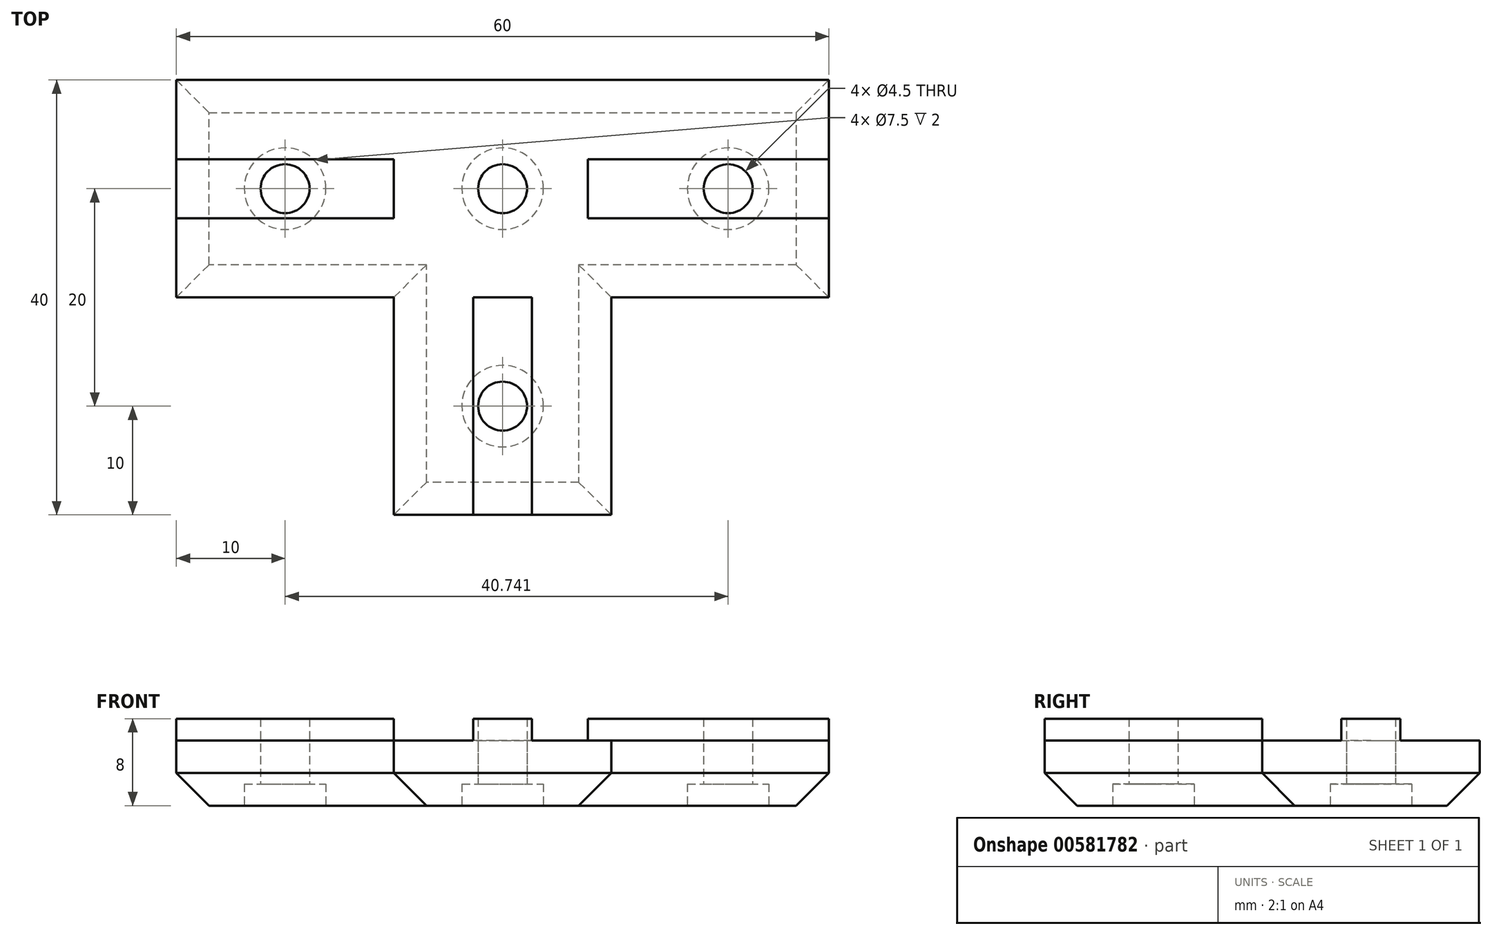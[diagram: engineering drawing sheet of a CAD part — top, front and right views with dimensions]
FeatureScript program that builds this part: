
annotation { "Feature Type Name" : "Feature", "Feature Type Description" : "" }
export const myFeature = defineFeature(function(context is Context, id is Id, definition is map)
    precondition{}
    {
        {
            var Q0;
            Q0=qCreatedBy(makeId("Top.planeOp"),FACE);
            var sketch = newSketch(context, id + "F0", { "sketchPlane" : qUnion([Q0])});
            skLineSegment(sketch, "E0", {"start": v(0, 0) * mm, "end": v(0, 20) * mm, "construction": true});
            skLineSegment(sketch, "E1", {"start": v(0, 0) * mm, "end": v(0, -20) * mm, "construction": true});
            skLineSegment(sketch, "E2", {"start": v(-10, 0) * mm, "end": v(-30, 0) * mm});
            skLineSegment(sketch, "E3", {"start": v(0, 20) * mm, "end": v(-30, 20) * mm});
            skLineSegment(sketch, "E4", {"start": v(-30, 20) * mm, "end": v(-30, 0) * mm});
            skLineSegment(sketch, "E5", {"start": v(0, 20) * mm, "end": v(30, 20) * mm});
            skLineSegment(sketch, "E6", {"start": v(30, 20) * mm, "end": v(30, 0) * mm});
            skLineSegment(sketch, "E7", {"start": v(30, 0) * mm, "end": v(10, 0) * mm});
            skLineSegment(sketch, "E8", {"start": v(0, -20) * mm, "end": v(10, -20) * mm});
            skLineSegment(sketch, "E9", {"start": v(10, -20) * mm, "end": v(10, 0) * mm});
            skLineSegment(sketch, "E10", {"start": v(0, -20) * mm, "end": v(-10, -20) * mm});
            skLineSegment(sketch, "E11", {"start": v(-10, -20) * mm, "end": v(-10, 0) * mm});
            skSolve(sketch);
        }
        {
            var Q0;
            Q0=qSketchRegion(id+"F0",true);
            extrude(context, id + "F1", {"entities" : qUnion([Q0]), "depth" : 6 * mm});
        }
        {
            var Q0;
            Q0=makeQuery(id+"F1.opExtrude","CAP_FACE",FACE,{"disambiguationData":[OSD([sQuery(id+"F0.wireOp",EDGE,"E2"),sQuery(id+"F0.wireOp",EDGE,"E3"),sQuery(id+"F0.wireOp",EDGE,"E4"),sQuery(id+"F0.wireOp",EDGE,"E5"),sQuery(id+"F0.wireOp",EDGE,"E6"),sQuery(id+"F0.wireOp",EDGE,"E7"),sQuery(id+"F0.wireOp",EDGE,"E8"),sQuery(id+"F0.wireOp",EDGE,"E9"),sQuery(id+"F0.wireOp",EDGE,"E10"),sQuery(id+"F0.wireOp",EDGE,"E11")])],"isStart":false});
            var sketch = newSketch(context, id + "F2", { "sketchPlane" : qUnion([Q0])});
            skLineSegment(sketch, "E12", {"start": v(-30, 10) * mm, "end": v(30, 10) * mm, "construction": true});
            skLineSegment(sketch, "E13", {"start": v(0, -20) * mm, "end": v(0, 0) * mm, "construction": true});
            skLineSegment(sketch, "E14", {"start": v(0, 0) * mm, "end": v(-2.71, 0) * mm});
            skLineSegment(sketch, "E15", {"start": v(-2.71, 0) * mm, "end": v(-2.7, -20) * mm});
            skLineSegment(sketch, "E16", {"start": v(2.71, -20) * mm, "end": v(2.71, 0) * mm});
            skLineSegment(sketch, "E17", {"start": v(2.71, 0) * mm, "end": v(0, 0) * mm});
            skLineSegment(sketch, "E18", {"start": v(-2.7, -20) * mm, "end": v(2.71, -20) * mm});
            skLineSegment(sketch, "E19", {"start": v(7.85, 10) * mm, "end": v(7.85, 12.71) * mm});
            skLineSegment(sketch, "E20", {"start": v(7.85, 12.71) * mm, "end": v(30, 12.71) * mm});
            skLineSegment(sketch, "E21", {"start": v(30, 12.71) * mm, "end": v(30, 7.3) * mm});
            skLineSegment(sketch, "E22", {"start": v(30, 7.3) * mm, "end": v(7.85, 7.29) * mm});
            skLineSegment(sketch, "E23", {"start": v(7.85, 7.29) * mm, "end": v(7.85, 10) * mm});
            skLineSegment(sketch, "E24", {"start": v(-30, 12.71) * mm, "end": v(-30, 7.29) * mm});
            skLineSegment(sketch, "E25", {"start": v(-30, 7.29) * mm, "end": v(-10, 7.29) * mm});
            skLineSegment(sketch, "E26", {"start": v(-10, 7.29) * mm, "end": v(-10, 12.71) * mm});
            skLineSegment(sketch, "E27", {"start": v(-10, 12.71) * mm, "end": v(-30, 12.71) * mm});
            skSolve(sketch);
        }
        {
            var Q0;
            Q0=qSketchRegion(id+"F2",true);
            extrude(context, id + "F3", {"entities" : qUnion([Q0]), "operationType" : NewBodyOperationType.ADD, "depth" : 2 * mm});
        }
        {
            var Q0;
            Q0=makeQuery(id+"F1.opExtrude","CAP_FACE",FACE,{"disambiguationData":[OSD([sQuery(id+"F0.wireOp",EDGE,"E2"),sQuery(id+"F0.wireOp",EDGE,"E3"),sQuery(id+"F0.wireOp",EDGE,"E4"),sQuery(id+"F0.wireOp",EDGE,"E5"),sQuery(id+"F0.wireOp",EDGE,"E6"),sQuery(id+"F0.wireOp",EDGE,"E7"),sQuery(id+"F0.wireOp",EDGE,"E8"),sQuery(id+"F0.wireOp",EDGE,"E9"),sQuery(id+"F0.wireOp",EDGE,"E10"),sQuery(id+"F0.wireOp",EDGE,"E11")])],"isStart":true});
            var sketch = newSketch(context, id + "F4", { "sketchPlane" : qUnion([Q0])});
            skCircle(sketch, "E28", {"center": v(-20, -10) * mm, "radius": 2.25 * mm});
            skCircle(sketch, "E29", {"center": v(0, -10) * mm, "radius": 2.25 * mm});
            skCircle(sketch, "E30", {"center": v(0, 10) * mm, "radius": 2.25 * mm});
            skCircle(sketch, "E31", {"center": v(20.74, -10) * mm, "radius": 2.25 * mm});
            skSolve(sketch);
        }
        {
            var Q0;
            Q0=qSketchRegion(id+"F4",true);
            extrude(context, id + "F5", {"entities" : qUnion([Q0]), "operationType" : NewBodyOperationType.REMOVE, "endBound" : BoundingType.THROUGH_ALL, "oppositeDirection" : true, "depth" : 25 * mm});
        }
        {
            var Q0;
            Q0=makeQuery(id+"F1.opExtrude","CAP_FACE",FACE,{"disambiguationData":[OSD([sQuery(id+"F0.wireOp",EDGE,"E2"),sQuery(id+"F0.wireOp",EDGE,"E3"),sQuery(id+"F0.wireOp",EDGE,"E4"),sQuery(id+"F0.wireOp",EDGE,"E5"),sQuery(id+"F0.wireOp",EDGE,"E6"),sQuery(id+"F0.wireOp",EDGE,"E7"),sQuery(id+"F0.wireOp",EDGE,"E8"),sQuery(id+"F0.wireOp",EDGE,"E9"),sQuery(id+"F0.wireOp",EDGE,"E10"),sQuery(id+"F0.wireOp",EDGE,"E11")])],"isStart":true});
            var sketch = newSketch(context, id + "F6", { "sketchPlane" : qUnion([Q0])});
            skCircle(sketch, "E32", {"center": v(0, 10) * mm, "radius": 3.75 * mm});
            skCircle(sketch, "E33", {"center": v(0, -10) * mm, "radius": 3.75 * mm});
            skCircle(sketch, "E34", {"center": v(20.74, -10) * mm, "radius": 3.75 * mm});
            skCircle(sketch, "E35", {"center": v(-20, -10) * mm, "radius": 3.75 * mm});
            skSolve(sketch);
        }
        {
            var Q0;
            Q0=qSketchRegion(id+"F6",true);
            extrude(context, id + "F7", {"entities" : qUnion([Q0]), "operationType" : NewBodyOperationType.REMOVE, "oppositeDirection" : true, "depth" : 2 * mm});
        }
        {
            var Q0;
            Q0=makeQuery(id+"F1.opExtrude","CAP_EDGE",EDGE,{"disambiguationData":[OSD([sQuery(id+"F0.wireOp",EDGE,"E11")])],"isStart":true});
            var Q1;
            Q1=makeQuery(id+"F1.opExtrude","CAP_EDGE",EDGE,{"disambiguationData":[OSD([sQuery(id+"F0.wireOp",EDGE,"E2")])],"isStart":true});
            var Q2;
            Q2=makeQuery(id+"F1.opExtrude","CAP_EDGE",EDGE,{"disambiguationData":[OSD([sQuery(id+"F0.wireOp",EDGE,"E9")])],"isStart":true});
            var Q3;
            Q3=makeQuery(id+"F1.opExtrude","CAP_EDGE",EDGE,{"disambiguationData":[OSD([sQuery(id+"F0.wireOp",EDGE,"E7")])],"isStart":true});
            var Q4;
            Q4=makeQuery(id+"F1.opExtrude","CAP_EDGE",EDGE,{"disambiguationData":[OSD([sQuery(id+"F0.wireOp",EDGE,"E3"),sQuery(id+"F0.wireOp",EDGE,"E5")])],"isStart":true});
            var Q5;
            Q5=makeQuery(id+"F1.opExtrude","CAP_EDGE",EDGE,{"disambiguationData":[OSD([sQuery(id+"F0.wireOp",EDGE,"E6")])],"isStart":true});
            var Q6;
            Q6=makeQuery(id+"F1.opExtrude","CAP_EDGE",EDGE,{"disambiguationData":[OSD([sQuery(id+"F0.wireOp",EDGE,"E4")])],"isStart":true});
            var Q7;
            Q7=makeQuery(id+"F1.opExtrude","CAP_EDGE",EDGE,{"disambiguationData":[OSD([sQuery(id+"F0.wireOp",EDGE,"E8"),sQuery(id+"F0.wireOp",EDGE,"E10")])],"isStart":true});
            chamfer(context, id + "F8", {"entities" : qUnion([Q0, Q1, Q2, Q3, Q4, Q5, Q6, Q7]), "width" : 3 * mm, "tangentPropagation" : true});
        }
    });
